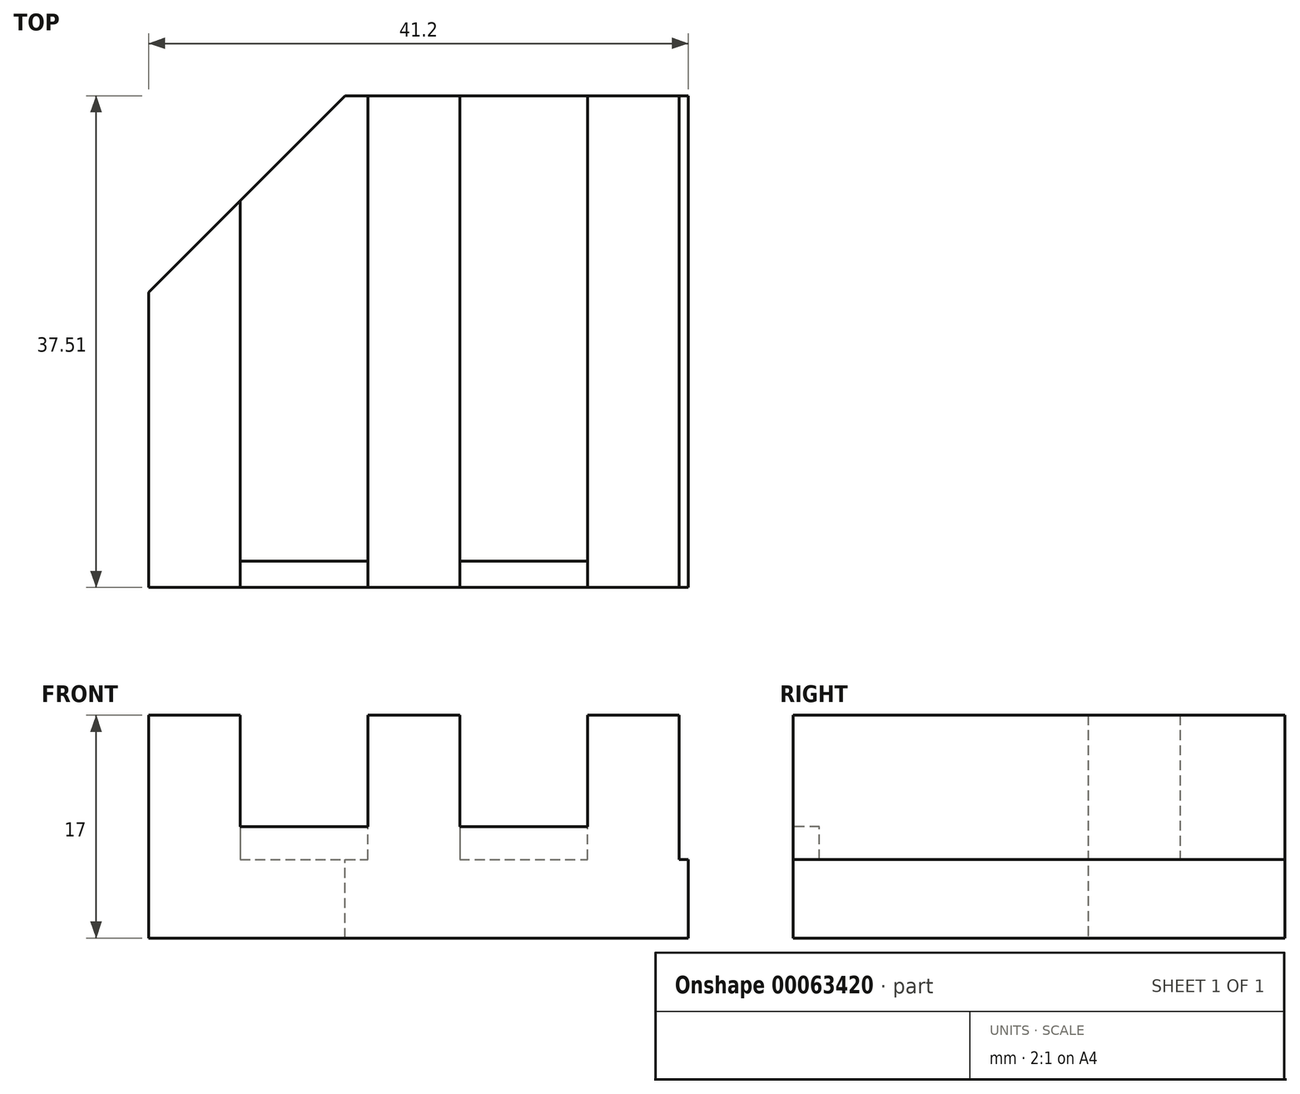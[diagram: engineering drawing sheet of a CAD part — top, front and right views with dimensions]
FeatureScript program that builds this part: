
annotation { "Feature Type Name" : "Feature", "Feature Type Description" : "" }
export const myFeature = defineFeature(function(context is Context, id is Id, definition is map)
    precondition{}
    {
        {
            var Q0;
            Q0=qCreatedBy(makeId("Front.planeOp"),FACE);
            var sketch = newSketch(context, id + "F0", { "sketchPlane" : qUnion([Q0])});
            skLineSegment(sketch, "E0", {"start": v(0, 0) * mm, "end": v(7, 0) * mm});
            skLineSegment(sketch, "E1", {"start": v(7, 0) * mm, "end": v(7, -11) * mm});
            skLineSegment(sketch, "E2", {"start": v(7, -11) * mm, "end": v(16.75, -11) * mm});
            skLineSegment(sketch, "E3", {"start": v(16.75, -11) * mm, "end": v(16.75, 0) * mm});
            skLineSegment(sketch, "E4.1.0.0", {"start": v(33.5, -11) * mm, "end": v(33.5, 0) * mm});
            skLineSegment(sketch, "E4.1.0.1", {"start": v(16.75, 0) * mm, "end": v(23.75, 0) * mm});
            skLineSegment(sketch, "E4.1.0.2", {"start": v(23.75, 0) * mm, "end": v(23.75, -11) * mm});
            skLineSegment(sketch, "E4.1.0.3", {"start": v(23.75, -11) * mm, "end": v(33.5, -11) * mm});
            skLineSegment(sketch, "E4.2.0.0", {"start": v(50.25, -11) * mm, "end": v(50.25, 0) * mm});
            skLineSegment(sketch, "E4.2.0.1", {"start": v(33.5, 0) * mm, "end": v(40.5, 0) * mm});
            skLineSegment(sketch, "E4.2.0.2", {"start": v(40.5, 0) * mm, "end": v(40.5, -11) * mm});
            skLineSegment(sketch, "E4.2.0.3", {"start": v(40.5, -11) * mm, "end": v(50.25, -11) * mm});
            skLineSegment(sketch, "E4.3.0.0", {"start": v(67, -11) * mm, "end": v(67, 0) * mm});
            skLineSegment(sketch, "E4.3.0.1", {"start": v(50.25, 0) * mm, "end": v(57.25, 0) * mm});
            skLineSegment(sketch, "E4.3.0.2", {"start": v(57.25, 0) * mm, "end": v(57.25, -11) * mm});
            skLineSegment(sketch, "E4.3.0.3", {"start": v(57.25, -11) * mm, "end": v(67, -11) * mm});
            skLineSegment(sketch, "E4.4.0.0", {"start": v(83.75, -11) * mm, "end": v(83.75, 0) * mm});
            skLineSegment(sketch, "E4.4.0.1", {"start": v(67, 0) * mm, "end": v(74, 0) * mm});
            skLineSegment(sketch, "E4.4.0.2", {"start": v(74, 0) * mm, "end": v(74, -11) * mm});
            skLineSegment(sketch, "E4.4.0.3", {"start": v(74, -11) * mm, "end": v(83.75, -11) * mm});
            skLineSegment(sketch, "E4.5.0.0", {"start": v(100.5, -11) * mm, "end": v(100.5, 0) * mm});
            skLineSegment(sketch, "E4.5.0.1", {"start": v(83.75, 0) * mm, "end": v(90.75, 0) * mm});
            skLineSegment(sketch, "E4.5.0.2", {"start": v(90.75, 0) * mm, "end": v(90.75, -11) * mm});
            skLineSegment(sketch, "E4.5.0.3", {"start": v(90.75, -11) * mm, "end": v(100.5, -11) * mm});
            skLineSegment(sketch, "E4.6.0.0", {"start": v(117.25, -11) * mm, "end": v(117.25, 0) * mm});
            skLineSegment(sketch, "E4.6.0.1", {"start": v(100.5, 0) * mm, "end": v(107.5, 0) * mm});
            skLineSegment(sketch, "E4.6.0.2", {"start": v(107.5, 0) * mm, "end": v(107.5, -11) * mm});
            skLineSegment(sketch, "E4.6.0.3", {"start": v(107.5, -11) * mm, "end": v(117.25, -11) * mm});
            skLineSegment(sketch, "E4.7.0.0", {"start": v(134, -11) * mm, "end": v(134, 0) * mm});
            skLineSegment(sketch, "E4.7.0.1", {"start": v(117.25, 0) * mm, "end": v(124.25, 0) * mm});
            skLineSegment(sketch, "E4.7.0.2", {"start": v(124.25, 0) * mm, "end": v(124.25, -11) * mm});
            skLineSegment(sketch, "E4.7.0.3", {"start": v(124.25, -11) * mm, "end": v(134, -11) * mm});
            skLineSegment(sketch, "E4.8.0.0", {"start": v(150.75, -11) * mm, "end": v(150.75, 0) * mm});
            skLineSegment(sketch, "E4.8.0.1", {"start": v(134, 0) * mm, "end": v(141, 0) * mm});
            skLineSegment(sketch, "E4.8.0.2", {"start": v(141, 0) * mm, "end": v(141, -11) * mm});
            skLineSegment(sketch, "E4.8.0.3", {"start": v(141, -11) * mm, "end": v(150.75, -11) * mm});
            skLineSegment(sketch, "E4.9.0.0", {"start": v(167.5, -11) * mm, "end": v(167.5, 0) * mm});
            skLineSegment(sketch, "E4.9.0.1", {"start": v(150.75, 0) * mm, "end": v(157.75, 0) * mm});
            skLineSegment(sketch, "E4.9.0.2", {"start": v(157.75, 0) * mm, "end": v(157.75, -11) * mm});
            skLineSegment(sketch, "E4.9.0.3", {"start": v(157.75, -11) * mm, "end": v(167.5, -11) * mm});
            skLineSegment(sketch, "E4.10.0.0", {"start": v(184.25, -11) * mm, "end": v(184.25, 0) * mm});
            skLineSegment(sketch, "E4.10.0.1", {"start": v(167.5, 0) * mm, "end": v(174.5, 0) * mm});
            skLineSegment(sketch, "E4.10.0.2", {"start": v(174.5, 0) * mm, "end": v(174.5, -11) * mm});
            skLineSegment(sketch, "E4.10.0.3", {"start": v(174.5, -11) * mm, "end": v(184.25, -11) * mm});
            skLineSegment(sketch, "E4.11.0.0", {"start": v(201, -11) * mm, "end": v(201, 0) * mm});
            skLineSegment(sketch, "E4.11.0.1", {"start": v(184.25, 0) * mm, "end": v(191.25, 0) * mm});
            skLineSegment(sketch, "E4.11.0.2", {"start": v(191.25, 0) * mm, "end": v(191.25, -11) * mm});
            skLineSegment(sketch, "E4.11.0.3", {"start": v(191.25, -11) * mm, "end": v(201, -11) * mm});
            skLineSegment(sketch, "E4.direction1", {"start": v(7, -11) * mm, "end": v(23.75, -11) * mm, "construction": true});
            skLineSegment(sketch, "E5", {"start": v(0, 0) * mm, "end": v(0, -17) * mm});
            skLineSegment(sketch, "E6", {"start": v(0, -17) * mm, "end": v(208, -17) * mm});
            skLineSegment(sketch, "E7", {"start": v(208, -17) * mm, "end": v(208, 0) * mm});
            skLineSegment(sketch, "E8", {"start": v(208, 0) * mm, "end": v(201, 0) * mm});
            skSolve(sketch);
        }
        {
            var Q0;
            Q0=qSketchRegion(id+"F0",true);
            extrude(context, id + "F1", {"entities" : qUnion([Q0]), "depth" : 100 * mm});
        }
        {
            var Q0;
            Q0=makeQuery(id+"F1.opExtrude","CAP_EDGE",EDGE,{"disambiguationData":[OSD([sQuery(id+"F0.wireOp",EDGE,"E5")])],"isStart":true});
            chamfer(context, id + "F2", {"entities" : qUnion([Q0]), "chamferType" : ChamferType.OFFSET_ANGLE, "width" : 15 * mm, "oppositeDirection" : false, "angle" : 45 * degree, "tangentPropagation" : true});
        }
        {
            var Q0;
            Q0=qCreatedBy(makeId("Top.planeOp"),FACE);
            var sketch = newSketch(context, id + "F3", { "sketchPlane" : qUnion([Q0])});
            skLineSegment(sketch, "E9.bottom", {"start": v(214.61, 11.07) * mm, "end": v(41.2, 11.07) * mm});
            skLineSegment(sketch, "E9.top", {"start": v(214.61, -116.84) * mm, "end": v(41.2, -116.84) * mm});
            skLineSegment(sketch, "E9.left", {"start": v(214.61, 11.07) * mm, "end": v(214.61, -116.84) * mm});
            skLineSegment(sketch, "E9.right", {"start": v(41.2, 11.07) * mm, "end": v(41.2, -116.84) * mm});
            skLineSegment(sketch, "E10.bottom", {"start": v(-10.45, -37.51) * mm, "end": v(49.81, -37.51) * mm});
            skLineSegment(sketch, "E10.top", {"start": v(-10.45, -116.84) * mm, "end": v(49.81, -116.84) * mm});
            skLineSegment(sketch, "E10.left", {"start": v(-10.45, -37.51) * mm, "end": v(-10.45, -116.84) * mm});
            skLineSegment(sketch, "E10.right", {"start": v(49.81, -37.51) * mm, "end": v(49.81, -116.84) * mm});
            skSolve(sketch);
        }
        {
            var Q0;
            Q0 = qSketchRegion(id + "F3", true);
            extrude(context, id + "F4", {"entities" : qUnion([Q0]), "operationType" : NewBodyOperationType.REMOVE, "endBound" : BoundingType.THROUGH_ALL, "oppositeDirection" : true, "depth" : 25 * mm});
        }
        {
            var Q0;
            Q0=makeQuery(id+"F4.boolean.opBoolean","COPY",FACE,{"derivedFrom":makeQuery(id+"F4.opExtrude","SWEPT_FACE",FACE,{"disambiguationData":[OSD([sQuery(id+"F3.wireOp",EDGE,"E10.bottom")])]})});
            var sketch = newSketch(context, id + "F5", { "sketchPlane" : qUnion([Q0])});
            skLineSegment(sketch, "E11.bottom", {"start": v(7, -11) * mm, "end": v(33.5, -11) * mm});
            skLineSegment(sketch, "E11.top", {"start": v(7, -8.5) * mm, "end": v(33.5, -8.5) * mm});
            skLineSegment(sketch, "E11.left", {"start": v(7, -11) * mm, "end": v(7, -8.5) * mm});
            skLineSegment(sketch, "E11.right", {"start": v(33.5, -11) * mm, "end": v(33.5, -8.5) * mm});
            skSolve(sketch);
        }
        {
            var Q0;
            Q0 = qSketchRegion(id + "F5", true);
            extrude(context, id + "F6", {"entities" : qUnion([Q0]), "operationType" : NewBodyOperationType.ADD, "oppositeDirection" : true, "depth" : 2 * mm});
        }
    });
